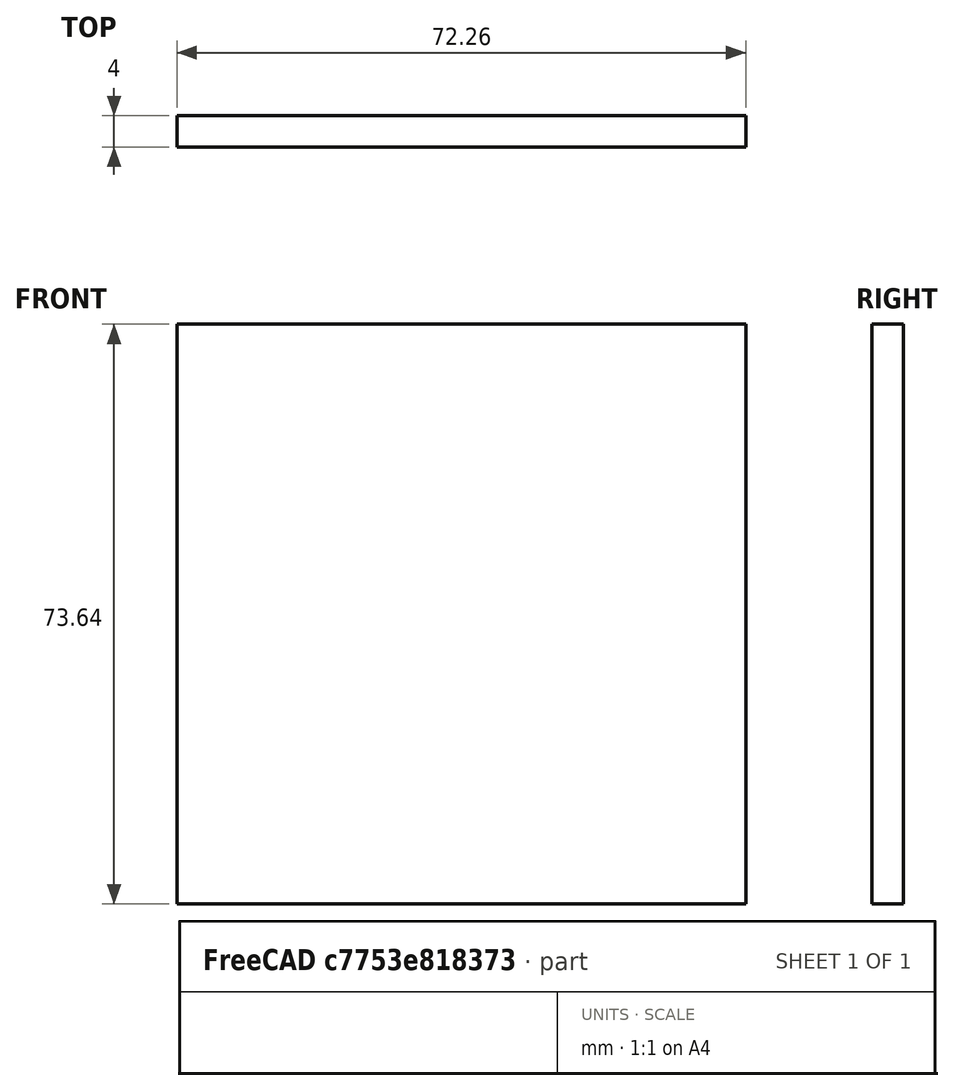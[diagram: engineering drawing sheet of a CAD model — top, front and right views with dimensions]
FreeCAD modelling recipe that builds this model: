
FCSTD DOCUMENT  (FreeCAD 0.20R29177 (Git))
Label: cubo
License: All rights reserved
LicenseURL: http://en.wikipedia.org/wiki/All_rights_reserved
objects: Sketcher::SketchObject×2, PartDesign::Body×2, Image::ImagePlane×1, PartDesign::Pad×1, Part::FeaturePython×1
note: 7 computed .brp shape members not serialized (recipe doc carries the construction recipe); baked Part::Feature solids carry a one-line shape summary decoded from their .brp

FEATURE [Image::ImagePlane] ImagePlane
  Placement = pos=(0,0,0) rot=(1,0,0;1.5708rad)
  XSize = 66.9788
  YSize = 68.204
FEATURE [Sketcher::SketchObject] Sketch
  FullyConstrained = false
  MapMode = 5
  Placement = pos=(0,0,0) rot=(1,0,0;1.5708rad)
  Support = -> [XZ_Plane]
  sketch-geometry (8):
    g0: LineSegment StartX=-33.1252 StartY=33.8157 StartZ=0 EndX=33.1252 EndY=33.8157 EndZ=0
    g1: LineSegment StartX=33.1252 StartY=33.8157 StartZ=0 EndX=33.1252 EndY=-33.8157 EndZ=0
    g2: LineSegment StartX=33.1252 StartY=-33.8157 StartZ=0 EndX=-33.1252 EndY=-33.8157 EndZ=0
    g3: LineSegment StartX=-33.1252 StartY=-33.8157 StartZ=0 EndX=-33.1252 EndY=33.8157 EndZ=0
    g4: LineSegment StartX=-36.1252 StartY=36.8157 StartZ=0 EndX=36.1252 EndY=36.8157 EndZ=0
    g5: LineSegment StartX=36.1252 StartY=36.8157 StartZ=0 EndX=36.1252 EndY=-36.8157 EndZ=0
    g6: LineSegment StartX=36.1252 StartY=-36.8157 StartZ=0 EndX=-36.1252 EndY=-36.8157 EndZ=0
    g7: LineSegment StartX=-36.1252 StartY=-36.8157 StartZ=0 EndX=-36.1252 EndY=36.8157 EndZ=0
  constraints (22):
    c: Coincident(g0,g1)
    c: Coincident(g1,g2)
    c: Coincident(g2,g3)
    c: Coincident(g3,g0)
    c: Horizontal(g0)
    c: Horizontal(g2)
    c: Vertical(g1)
    c: Vertical(g3)
    c: Symmetric(g1,g0,g-1)
    c: DistanceX(g0,g0) = 66.2505
    c: Coincident(g4,g5)
    c: Coincident(g5,g6)
    c: Coincident(g6,g7)
    c: Coincident(g7,g4)
    c: Horizontal(g4)
    c: Horizontal(g6)
    c: Vertical(g5)
    c: Vertical(g7)
    c: Symmetric(g5,g4,g-1)
    c: DistanceX(g4,g0) = 3
    c: DistanceY(g0,g4) = 3
    c: DistanceY(g1,g1) = 67.6314
FEATURE [PartDesign::Pad] Pad
  Direction = (0,-1,2e-16)
  Length = 4
  Length2 = 10
  Placement = pos=(0,0,0) rot=(1,0,0;1.5708rad)
  Profile = -> Sketch
  ReferenceAxis = -> Sketch [N_Axis]
  Refine = true
  Type = 0
FEATURE [PartDesign::Body] Body
  Group = -> [Sketch,Pad]
  Origin = -> Origin
  Tip = -> Pad
FEATURE [Sketcher::SketchObject] Sketch002
  ExternalGeometry = -> [Pad]
  FullyConstrained = false
  MapMode = 5
  Placement = pos=(0,-4,9e-16) rot=(1,0,0;1.5708rad)
  Support = -> [Pad]
  sketch-geometry (9):
    g0: LineSegment StartX=-33.9252 StartY=34.8157 StartZ=0 EndX=34.1252 EndY=34.8157 EndZ=0
    g1: LineSegment StartX=34.1252 StartY=34.8157 StartZ=0 EndX=34.1252 EndY=-34.8157 EndZ=0
    g2: LineSegment StartX=34.1252 StartY=-34.8157 StartZ=0 EndX=-33.9252 EndY=-34.8157 EndZ=0
    g3: LineSegment StartX=-33.9252 StartY=-34.8157 StartZ=0 EndX=-33.9252 EndY=34.8157 EndZ=0
    g4: LineSegment StartX=-32.9252 StartY=33.8157 StartZ=0 EndX=-25.9252 EndY=33.8157 EndZ=0
    g5: LineSegment StartX=-25.9252 StartY=33.8157 StartZ=0 EndX=-25.9252 EndY=26.8157 EndZ=0
    g6: LineSegment StartX=-25.9252 StartY=26.8157 StartZ=0 EndX=-32.9252 EndY=26.8157 EndZ=0
    g7: LineSegment StartX=-32.9252 StartY=26.8157 StartZ=0 EndX=-32.9252 EndY=33.8157 EndZ=0
    g8: LineSegment StartX=-25.9252 StartY=26.8157 StartZ=0 EndX=-17.8279 EndY=26.8157 EndZ=0
  constraints (26):
    c: Coincident(g0,g1)
    c: Coincident(g1,g2)
    c: Coincident(g2,g3)
    c: Coincident(g3,g0)
    c: Horizontal(g0)
    c: Horizontal(g2)
    c: Vertical(g1)
    c: Vertical(g3)
    c: DistanceY(g-4,g1) = 2
    c: DistanceX(g0,g-3) = 2
    c: Coincident(g4,g5)
    c: Coincident(g5,g6)
    c: Coincident(g6,g7)
    c: Horizontal(g4)
    c: Horizontal(g6)
    c: Vertical(g5)
    c: Vertical(g7)
    c: Equal(g5,g4)
    c: DistanceX(g4,g4) = 7
    c: Coincident(g8,g5)
    c: Horizontal(g8)
    c: Coincident(g7,g4)
    c: DistanceX(g0,g4) = 1
    c: DistanceY(g4,g0) = 1
    c: DistanceY(g0,g-3) = 2
    c: DistanceX(g-4,g2) = 2.2
FEATURE [PartDesign::Body] Body001
  Group = -> [Sketch002]
  Origin = -> Origin001
FEATURE [Part::FeaturePython] Array  # Draft array (typed FeaturePython)
  Angle = 360
  ArrayType = 0
  Axis = (0,0,1)
  Base = -> Sketch002
  Center = (0,0,0)
  Fuse = true
  IntervalAxis = (0,0,0)
  IntervalX = (8,0,0)
  IntervalY = (0,8,0)
  IntervalZ = (0,0,100)
  NumberCircles = 3
  NumberPolar = 5
  NumberX = 8
  NumberY = 8
  NumberZ = 1
  RadialDistance = 50
  Symmetry = 1
  TangentialDistance = 25
